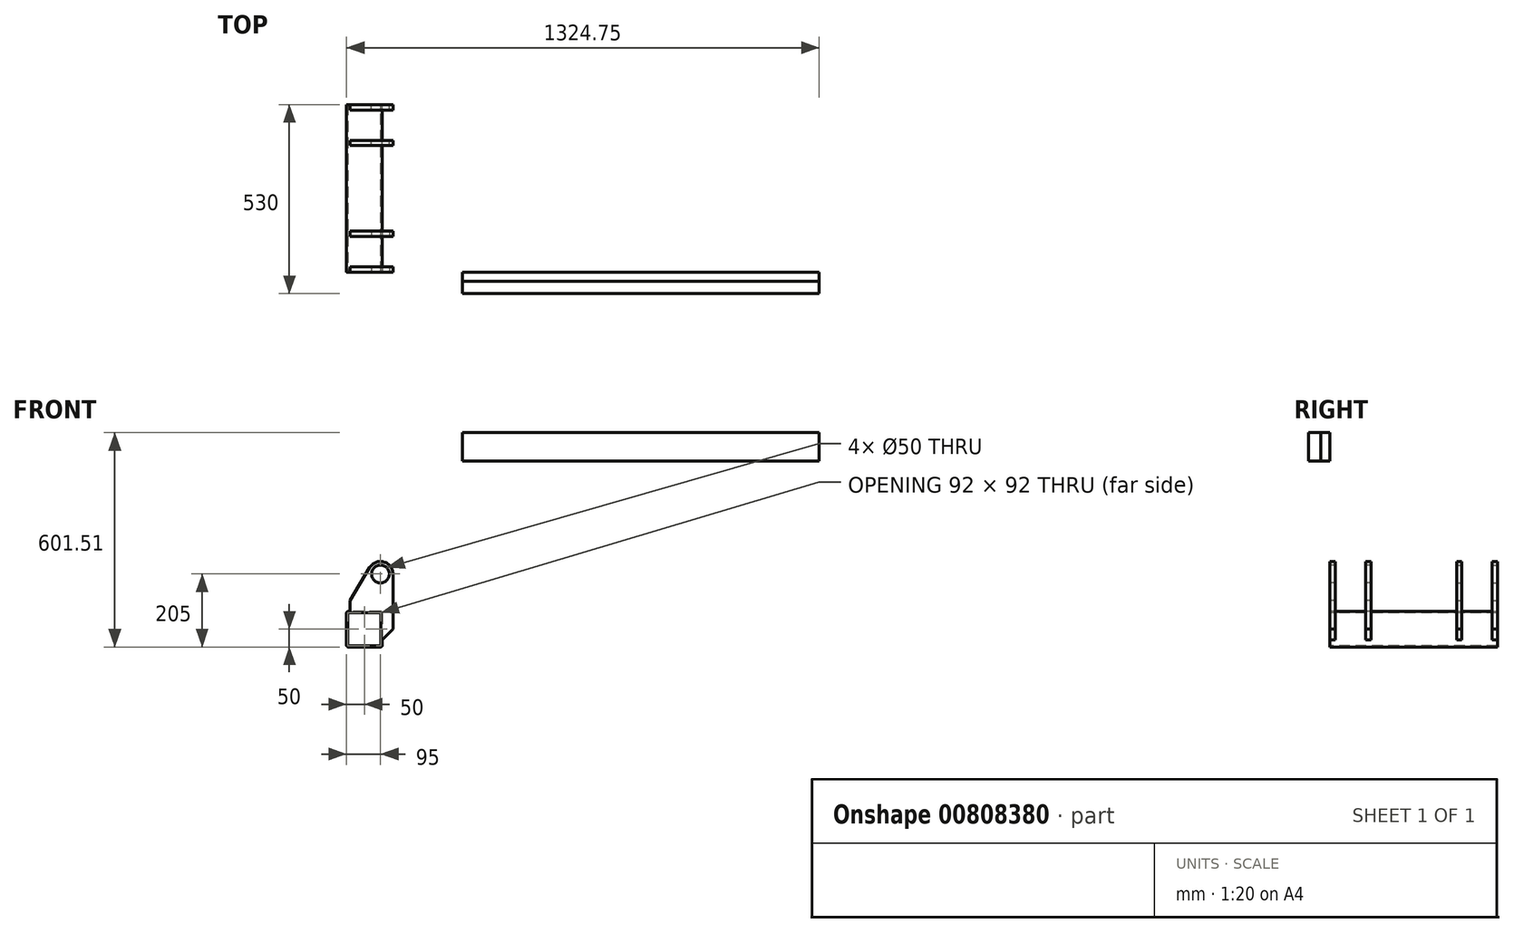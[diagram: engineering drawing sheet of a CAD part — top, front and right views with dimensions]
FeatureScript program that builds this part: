
annotation { "Feature Type Name" : "Feature", "Feature Type Description" : "" }
export const myFeature = defineFeature(function(context is Context, id is Id, definition is map)
    precondition{}
    {
        {
            var Q0;
            Q0=qCreatedBy(makeId("Front.planeOp"),FACE);
            var sketch = newSketch(context, id + "F0", { "sketchPlane" : qUnion([Q0])});
            skLineSegment(sketch, "E0.bottom", {"start": v(45, 50) * mm, "end": v(-45, 50) * mm});
            skLineSegment(sketch, "E0.top", {"start": v(45, -50) * mm, "end": v(-45, -50) * mm});
            skLineSegment(sketch, "E0.left", {"start": v(50, 45) * mm, "end": v(50, -45) * mm});
            skLineSegment(sketch, "E0.right", {"start": v(-50, 45) * mm, "end": v(-50, -45) * mm});
            skPoint(sketch, "E0.middle", {"position": v(0, 0) * mm});
            skPoint(sketch, "E1.visualSharp", {"position": v(-50, 50) * mm});
            skArc(sketch, "E1.filletArc", {"start": v(-45, 50) * mm, "mid": v(-48.54, 48.54) * mm, "end": v(-50, 45) * mm});
            skPoint(sketch, "E2.visualSharp", {"position": v(50, 50) * mm});
            skArc(sketch, "E2.filletArc", {"start": v(50, 45) * mm, "mid": v(48.54, 48.54) * mm, "end": v(45, 50) * mm});
            skPoint(sketch, "E3.visualSharp", {"position": v(50, -50) * mm});
            skArc(sketch, "E3.filletArc", {"start": v(45, -50) * mm, "mid": v(48.54, -48.54) * mm, "end": v(50, -45) * mm});
            skPoint(sketch, "E4.visualSharp", {"position": v(-50, -50) * mm});
            skArc(sketch, "E4.filletArc", {"start": v(-50, -45) * mm, "mid": v(-48.54, -48.54) * mm, "end": v(-45, -50) * mm});
            skLineSegment(sketch, "E5", {"start": v(80, 0) * mm, "end": v(80, 155) * mm});
            skLineSegment(sketch, "E6", {"start": v(-40.38, 80) * mm, "end": v(-40.38, 50) * mm});
            skArc(sketch, "E7", {"start": v(80, 155) * mm, "mid": v(54.28, 188.75) * mm, "end": v(14.93, 172.9) * mm});
            skPoint(sketch, "E8.orphan", {"position": v(80, 190) * mm});
            skLineSegment(sketch, "E9", {"start": v(-40.38, 80) * mm, "end": v(14.93, 172.9) * mm});
            skPoint(sketch, "E10", {"position": v(80, 0) * mm});
            skLineSegment(sketch, "E11", {"start": v(80, 0) * mm, "end": v(50, -30) * mm});
            skCircle(sketch, "E12", {"center": v(45, 155) * mm, "radius": 25 * mm});
            skLineSegment(sketch, "E13.bottom", {"start": v(274.75, 471.5) * mm, "end": v(1274.75, 471.5) * mm});
            skLineSegment(sketch, "E13.top", {"start": v(274.75, 551.5) * mm, "end": v(1274.75, 551.5) * mm});
            skLineSegment(sketch, "E13.left", {"start": v(274.75, 471.5) * mm, "end": v(274.75, 551.5) * mm});
            skLineSegment(sketch, "E13.right", {"start": v(1274.75, 471.5) * mm, "end": v(1274.75, 551.5) * mm});
            skSolve(sketch);
        }
        {
            var Q0;
            Q0=makeQuery(id+"F0.imprint","IMPRINT",FACE,{"disambiguationData":[TD([[makeQuery(id+"F0.imprint","IMPRINT",EDGE,{"derivedFrom":sQuery(id+"F0.wireOp",EDGE,"E0.bottom")}),1.0]])]});
            extrude(context, id + "F1", {"entities" : qUnion([Q0]), "oppositeDirection" : true, "depth" : 235 * mm, "offsetDistance" : 25 * mm});
        }
        {
            var Q0;
            Q0=makeQuery(id+"F1.opExtrude","CAP_FACE",FACE,{"disambiguationData":[OSD([sQuery(id+"F0.wireOp",EDGE,"E0.bottom"),sQuery(id+"F0.wireOp",EDGE,"E0.top"),sQuery(id+"F0.wireOp",EDGE,"E0.left"),sQuery(id+"F0.wireOp",EDGE,"E0.right"),sQuery(id+"F0.wireOp",EDGE,"E1.filletArc"),sQuery(id+"F0.wireOp",EDGE,"E2.filletArc"),sQuery(id+"F0.wireOp",EDGE,"E3.filletArc"),sQuery(id+"F0.wireOp",EDGE,"E4.filletArc")])],"isStart":true});
            var Q1;
            Q1=makeQuery(id+"F1.opExtrude","CAP_FACE",FACE,{"disambiguationData":[OSD([sQuery(id+"F0.wireOp",EDGE,"E0.bottom"),sQuery(id+"F0.wireOp",EDGE,"E0.top"),sQuery(id+"F0.wireOp",EDGE,"E0.left"),sQuery(id+"F0.wireOp",EDGE,"E0.right"),sQuery(id+"F0.wireOp",EDGE,"E1.filletArc"),sQuery(id+"F0.wireOp",EDGE,"E2.filletArc"),sQuery(id+"F0.wireOp",EDGE,"E3.filletArc"),sQuery(id+"F0.wireOp",EDGE,"E4.filletArc")])],"isStart":false});
            shell(context, id + "F2", {"entities" : qUnion([Q0, Q1]), "thickness" : 4 * mm});
        }
        {
            var Q0;
            {var subQ0=sQuery(id+"F0.wireOp",EDGE,"E2.filletArc");Q0=makeQuery(id+"F0.imprint","IMPRINT",FACE,{"disambiguationData":[TD([[makeQuery(id+"F0.imprint","IMPRINT",EDGE,{"derivedFrom":subQ0}),-1.0]])]});}
            extrude(context, id + "F3", {"entities" : qUnion([Q0]), "oppositeDirection" : true, "depth" : 15 * mm, "offsetDistance" : 25 * mm});
        }
        {
            var Q0;
            Q0=makeQuery(id+"F3.opExtrude","SWEPT_BODY",BODY,{"disambiguationData":[OSD([sQuery(id+"F0.wireOp",EDGE,"E0.bottom"),sQuery(id+"F0.wireOp",EDGE,"E0.left"),sQuery(id+"F0.wireOp",EDGE,"E2.filletArc"),sQuery(id+"F0.wireOp",EDGE,"E5"),sQuery(id+"F0.wireOp",EDGE,"E6"),sQuery(id+"F0.wireOp",EDGE,"E7"),sQuery(id+"F0.wireOp",EDGE,"E9"),sQuery(id+"F0.wireOp",EDGE,"E11"),sQuery(id+"F0.wireOp",EDGE,"E12")])]});
            var Q1;
            Q1=makeQuery(id+"F3.opExtrude","CAP_FACE",FACE,{"disambiguationData":[OSD([sQuery(id+"F0.wireOp",EDGE,"E0.bottom"),sQuery(id+"F0.wireOp",EDGE,"E0.left"),sQuery(id+"F0.wireOp",EDGE,"E2.filletArc"),sQuery(id+"F0.wireOp",EDGE,"E5"),sQuery(id+"F0.wireOp",EDGE,"E6"),sQuery(id+"F0.wireOp",EDGE,"E7"),sQuery(id+"F0.wireOp",EDGE,"E9"),sQuery(id+"F0.wireOp",EDGE,"E11"),sQuery(id+"F0.wireOp",EDGE,"E12")])],"isStart":false});
            transform(context, id + "F4", {"entities" : qUnion([Q0]), "transformType" : TransformType.TRANSLATION_DISTANCE, "transformDirection" : qUnion([Q1]), "distance" : 100 * mm, "makeCopy" : true});
        }
        {
            var Q0;
            Q0=makeQuery(id+"F1.opExtrude","SWEPT_BODY",BODY,{"disambiguationData":[OSD([sQuery(id+"F0.wireOp",EDGE,"E0.bottom"),sQuery(id+"F0.wireOp",EDGE,"E0.top"),sQuery(id+"F0.wireOp",EDGE,"E0.left"),sQuery(id+"F0.wireOp",EDGE,"E0.right"),sQuery(id+"F0.wireOp",EDGE,"E1.filletArc"),sQuery(id+"F0.wireOp",EDGE,"E2.filletArc"),sQuery(id+"F0.wireOp",EDGE,"E3.filletArc"),sQuery(id+"F0.wireOp",EDGE,"E4.filletArc")])]});
            var Q1;
            Q1=makeQuery(id+"F3.opExtrude","SWEPT_BODY",BODY,{"disambiguationData":[OSD([sQuery(id+"F0.wireOp",EDGE,"E0.bottom"),sQuery(id+"F0.wireOp",EDGE,"E0.left"),sQuery(id+"F0.wireOp",EDGE,"E2.filletArc"),sQuery(id+"F0.wireOp",EDGE,"E5"),sQuery(id+"F0.wireOp",EDGE,"E6"),sQuery(id+"F0.wireOp",EDGE,"E7"),sQuery(id+"F0.wireOp",EDGE,"E9"),sQuery(id+"F0.wireOp",EDGE,"E11"),sQuery(id+"F0.wireOp",EDGE,"E12")])]});
            var Q2;
            Q2=makeQuery(id+"F4.opPattern","COPY",BODY,{"derivedFrom":makeQuery(id+"F3.opExtrude","SWEPT_BODY",BODY,{"disambiguationData":[OSD([sQuery(id+"F0.wireOp",EDGE,"E0.bottom"),sQuery(id+"F0.wireOp",EDGE,"E0.left"),sQuery(id+"F0.wireOp",EDGE,"E2.filletArc"),sQuery(id+"F0.wireOp",EDGE,"E5"),sQuery(id+"F0.wireOp",EDGE,"E6"),sQuery(id+"F0.wireOp",EDGE,"E7"),sQuery(id+"F0.wireOp",EDGE,"E9"),sQuery(id+"F0.wireOp",EDGE,"E11"),sQuery(id+"F0.wireOp",EDGE,"E12")])]}),"instanceName":"1"});
            var Q3;
            Q3=makeQuery(id+"F1.opExtrude","CAP_FACE",FACE,{"disambiguationData":[OSD([sQuery(id+"F0.wireOp",EDGE,"E0.bottom"),sQuery(id+"F0.wireOp",EDGE,"E0.top"),sQuery(id+"F0.wireOp",EDGE,"E0.left"),sQuery(id+"F0.wireOp",EDGE,"E0.right"),sQuery(id+"F0.wireOp",EDGE,"E1.filletArc"),sQuery(id+"F0.wireOp",EDGE,"E2.filletArc"),sQuery(id+"F0.wireOp",EDGE,"E3.filletArc"),sQuery(id+"F0.wireOp",EDGE,"E4.filletArc")])],"isStart":false});
            mirror(context, id + "F5", {"operationType" : NewBodyOperationType.ADD, "entities" : qUnion([Q0, Q1, Q2]), "mirrorPlane" : qUnion([Q3])});
        }
        {
            var Q0;
            Q0=makeQuery(id+"F0.imprint","IMPRINT",FACE,{"disambiguationData":[TD([[makeQuery(id+"F0.imprint","IMPRINT",EDGE,{"derivedFrom":sQuery(id+"F0.wireOp",EDGE,"E13.bottom")}),1.0]])]});
            extrude(context, id + "F6", {"entities" : qUnion([Q0]), "depth" : 60 * mm, "offsetDistance" : 25 * mm});
        }
        {
            var Q0;
            Q0=makeQuery(id+"F0.imprint","IMPRINT",FACE,{"disambiguationData":[TD([[makeQuery(id+"F0.imprint","IMPRINT",EDGE,{"derivedFrom":sQuery(id+"F0.wireOp",EDGE,"E13.bottom")}),1.0]])]});
            extrude(context, id + "F7", {"entities" : qUnion([Q0]), "depth" : 25 * mm, "offsetDistance" : 25 * mm});
        }
    });
